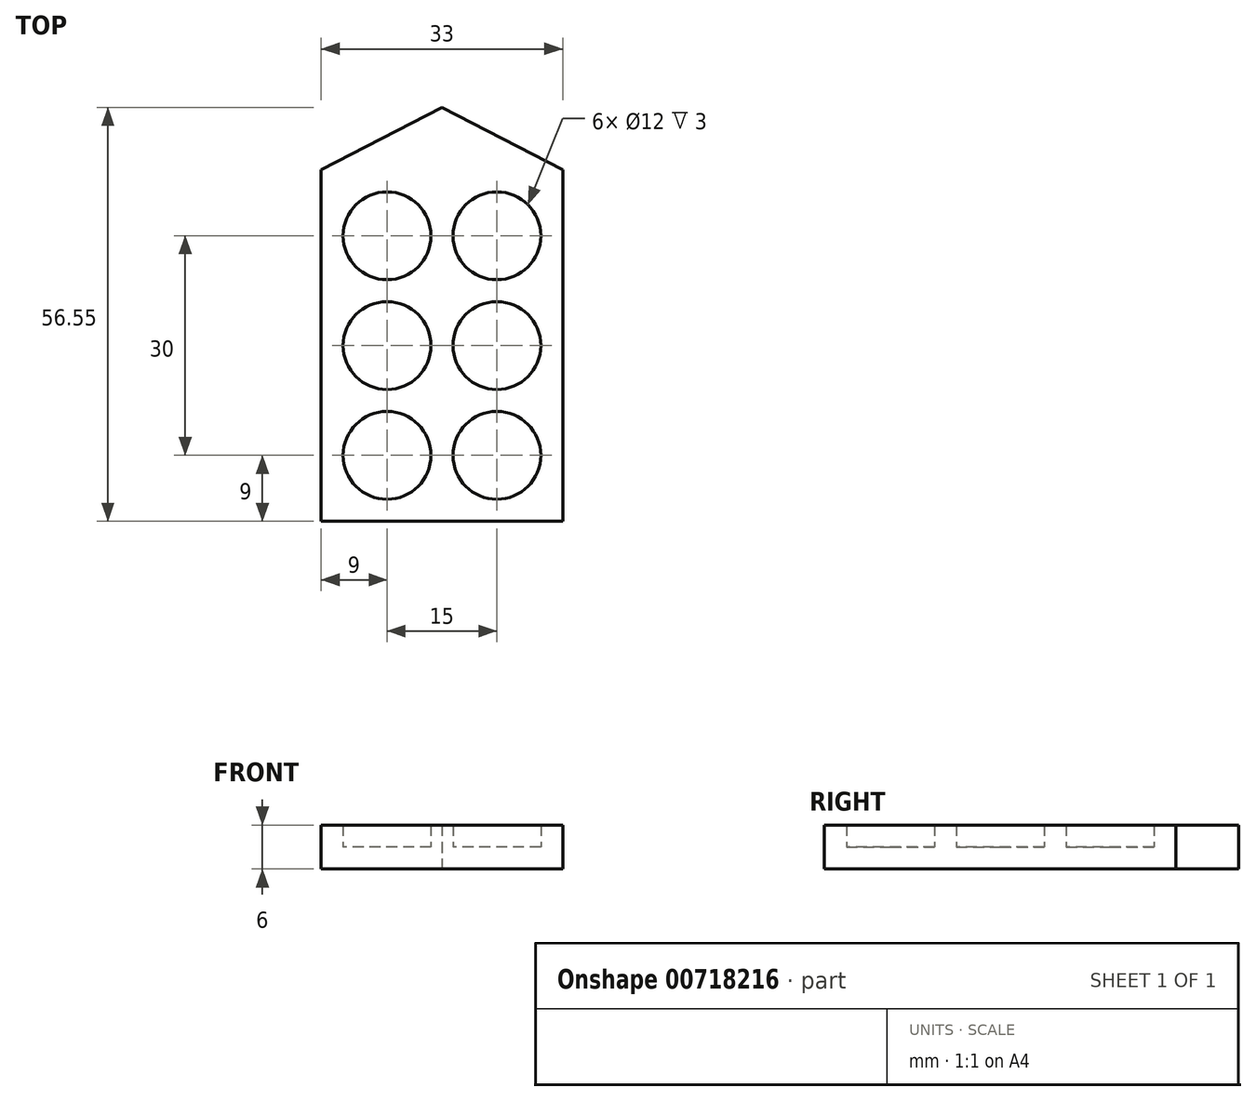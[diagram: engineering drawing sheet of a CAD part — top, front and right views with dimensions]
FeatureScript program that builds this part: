
annotation { "Feature Type Name" : "Feature", "Feature Type Description" : "" }
export const myFeature = defineFeature(function(context is Context, id is Id, definition is map)
    precondition{}
    {
        {
            var Q0;
            Q0=qCreatedBy(makeId("Top.planeOp"),FACE);
            var sketch = newSketch(context, id + "F0", { "sketchPlane" : qUnion([Q0])});
            skCircle(sketch, "E0", {"center": v(0, 0) * mm, "radius": 6 * mm});
            skCircle(sketch, "E1", {"center": v(15, 0) * mm, "radius": 6 * mm});
            skCircle(sketch, "E2", {"center": v(0, 15) * mm, "radius": 6 * mm});
            skCircle(sketch, "E3", {"center": v(15, 15) * mm, "radius": 6 * mm});
            skCircle(sketch, "E4", {"center": v(0, 30) * mm, "radius": 6 * mm});
            skCircle(sketch, "E5", {"center": v(15, 30) * mm, "radius": 6 * mm});
            skLineSegment(sketch, "E6.bottom", {"start": v(-9, 39) * mm, "end": v(24, 39) * mm, "construction": true});
            skLineSegment(sketch, "E6.top", {"start": v(-9, -9) * mm, "end": v(24, -9) * mm});
            skLineSegment(sketch, "E6.left", {"start": v(-9, 39) * mm, "end": v(-9, -9) * mm});
            skLineSegment(sketch, "E6.right", {"start": v(24, 39) * mm, "end": v(24, -9) * mm});
            skLineSegment(sketch, "E7", {"start": v(7.5, 39) * mm, "end": v(7.5, 47.55) * mm, "construction": true});
            skLineSegment(sketch, "E8", {"start": v(24, 39) * mm, "end": v(7.5, 47.55) * mm});
            skLineSegment(sketch, "E9", {"start": v(-9, 39) * mm, "end": v(7.5, 47.55) * mm});
            skSolve(sketch);
        }
        {
            var Q0;
            Q0 = qSketchRegion(id + "F0", true);
            extrude(context, id + "F1", {"entities" : qUnion([Q0]), "depth" : 3 * mm, "offsetDistance" : 25 * mm});
        }
        {
            var Q0;
            Q0=makeQuery(id+"F0.imprint","IMPRINT",FACE,{"disambiguationData":[TD([[makeQuery(id+"F0.imprint","IMPRINT",EDGE,{"derivedFrom":sQuery(id+"F0.wireOp",EDGE,"E0")}),-1.0]])]});
            var Q1;
            Q1=makeQuery(id+"F0.imprint","IMPRINT",FACE,{"disambiguationData":[TD([[makeQuery(id+"F0.imprint","IMPRINT",EDGE,{"derivedFrom":sQuery(id+"F0.wireOp",EDGE,"E4")}),1.0]])]});
            var Q2;
            Q2=makeQuery(id+"F0.imprint","IMPRINT",FACE,{"disambiguationData":[TD([[makeQuery(id+"F0.imprint","IMPRINT",EDGE,{"derivedFrom":sQuery(id+"F0.wireOp",EDGE,"E2")}),1.0]])]});
            var Q3;
            Q3=makeQuery(id+"F0.imprint","IMPRINT",FACE,{"disambiguationData":[TD([[makeQuery(id+"F0.imprint","IMPRINT",EDGE,{"derivedFrom":sQuery(id+"F0.wireOp",EDGE,"E0")}),1.0]])]});
            var Q4;
            Q4=makeQuery(id+"F0.imprint","IMPRINT",FACE,{"disambiguationData":[TD([[makeQuery(id+"F0.imprint","IMPRINT",EDGE,{"derivedFrom":sQuery(id+"F0.wireOp",EDGE,"E1")}),1.0]])]});
            var Q5;
            Q5=makeQuery(id+"F0.imprint","IMPRINT",FACE,{"disambiguationData":[TD([[makeQuery(id+"F0.imprint","IMPRINT",EDGE,{"derivedFrom":sQuery(id+"F0.wireOp",EDGE,"E3")}),1.0]])]});
            var Q6;
            Q6=makeQuery(id+"F0.imprint","IMPRINT",FACE,{"disambiguationData":[TD([[makeQuery(id+"F0.imprint","IMPRINT",EDGE,{"derivedFrom":sQuery(id+"F0.wireOp",EDGE,"E5")}),1.0]])]});
            extrude(context, id + "F2", {"entities" : qUnion([Q0, Q1, Q2, Q3, Q4, Q5, Q6]), "operationType" : NewBodyOperationType.ADD, "oppositeDirection" : true, "depth" : 3 * mm, "offsetDistance" : 25 * mm});
        }
    });
